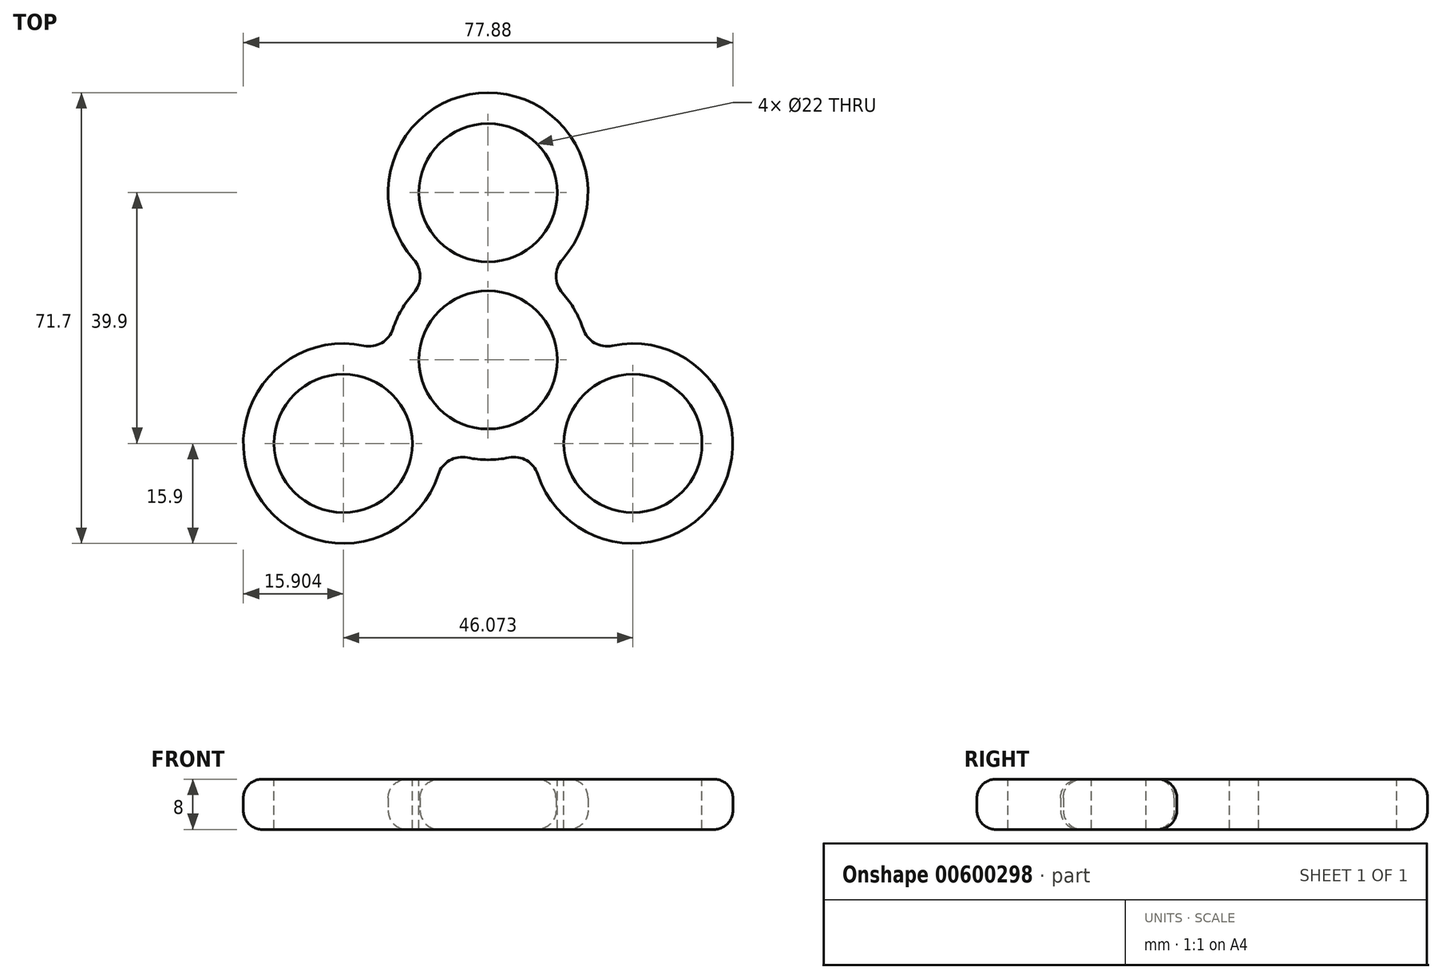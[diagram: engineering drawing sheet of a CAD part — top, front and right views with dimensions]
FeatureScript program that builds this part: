
annotation { "Feature Type Name" : "Feature", "Feature Type Description" : "" }
export const myFeature = defineFeature(function(context is Context, id is Id, definition is map)
    precondition{}
    {
        {
            var Q0;
            Q0=qCreatedBy(makeId("Top.planeOp"),FACE);
            var sketch = newSketch(context, id + "F0", { "sketchPlane" : qUnion([Q0])});
            skCircle(sketch, "E0", {"center": v(0, 0) * mm, "radius": 42.5 * mm, "construction": true});
            skArc(sketch, "E1", {"start": v(-11.83, 15.97) * mm, "mid": v(0, 42.5) * mm, "end": v(11.83, 15.97) * mm});
            skArc(sketch, "E2", {"start": v(19.75, 2.26) * mm, "mid": v(36.8, -21.25) * mm, "end": v(7.92, -18.23) * mm});
            skArc(sketch, "E3", {"start": v(-19.75, 2.26) * mm, "mid": v(-36.8, -21.25) * mm, "end": v(-7.92, -18.23) * mm});
            skLineSegment(sketch, "E4", {"start": v(0, 26.6) * mm, "end": v(0, 0) * mm, "construction": true});
            skLineSegment(sketch, "E5", {"start": v(0, 0) * mm, "end": v(-23.04, -13.3) * mm, "construction": true});
            skLineSegment(sketch, "E6", {"start": v(0, 0) * mm, "end": v(23.04, -13.3) * mm, "construction": true});
            skLineSegment(sketch, "E7", {"start": v(0, -53.2) * mm, "end": v(-46.07, 26.6) * mm, "construction": true});
            skLineSegment(sketch, "E8", {"start": v(0, -53.2) * mm, "end": v(46.07, 26.6) * mm, "construction": true});
            skLineSegment(sketch, "E9", {"start": v(-46.07, 26.6) * mm, "end": v(46.07, 26.6) * mm, "construction": true});
            skArc(sketch, "E10", {"start": v(-11.83, 15.97) * mm, "mid": v(-10.8, 13.3) * mm, "end": v(-11.83, 10.63) * mm});
            skArc(sketch, "E11", {"start": v(-19.75, 2.26) * mm, "mid": v(-16.92, 2.7) * mm, "end": v(-15.12, 4.93) * mm});
            skArc(sketch, "E12", {"start": v(11.83, 15.97) * mm, "mid": v(10.8, 13.3) * mm, "end": v(11.83, 10.63) * mm});
            skArc(sketch, "E13", {"start": v(19.75, 2.26) * mm, "mid": v(16.92, 2.7) * mm, "end": v(15.12, 4.93) * mm});
            skArc(sketch, "E14", {"start": v(11.83, 10.63) * mm, "mid": v(13.77, 7.95) * mm, "end": v(15.12, 4.93) * mm});
            skArc(sketch, "E15", {"start": v(-7.92, -18.23) * mm, "mid": v(-6.12, -16) * mm, "end": v(-3.29, -15.56) * mm});
            skArc(sketch, "E16", {"start": v(7.92, -18.23) * mm, "mid": v(6.12, -16) * mm, "end": v(3.29, -15.56) * mm});
            skArc(sketch, "E17", {"start": v(-3.29, -15.56) * mm, "mid": v(0, -15.9) * mm, "end": v(3.29, -15.56) * mm});
            skArc(sketch, "E18", {"start": v(-15.12, 4.93) * mm, "mid": v(-13.77, 7.95) * mm, "end": v(-11.83, 10.63) * mm});
            skSolve(sketch);
        }
        {
            var Q0;
            Q0 = qSketchRegion(id + "F0", true);
            extrude(context, id + "F1", {"entities" : qUnion([Q0]), "endBound" : BoundingType.SYMMETRIC, "depth" : 8 * mm, "offsetDistance" : 25 * mm});
        }
        {
            var Q0;
            Q0=qCreatedBy(makeId("Top.planeOp"),FACE);
            var sketch = newSketch(context, id + "F2", { "sketchPlane" : qUnion([Q0])});
            skLineSegment(sketch, "E19.0", {"start": v(-11.83, 15.97) * mm, "end": v(-11.83, 15.97) * mm});
            skLineSegment(sketch, "E20.0", {"start": v(-19.75, 2.26) * mm, "end": v(-19.75, 2.26) * mm});
            skLineSegment(sketch, "E21.0", {"start": v(19.75, 2.26) * mm, "end": v(19.75, 2.26) * mm});
            skCircle(sketch, "E22", {"center": v(0, 26.6) * mm, "radius": 11 * mm});
            skCircle(sketch, "E23", {"center": v(-23.04, -13.3) * mm, "radius": 11 * mm});
            skCircle(sketch, "E24", {"center": v(23.04, -13.3) * mm, "radius": 11 * mm});
            skCircle(sketch, "E25", {"center": v(0, 0) * mm, "radius": 11 * mm});
            skSolve(sketch);
        }
        {
            var Q0;
            Q0 = qSketchRegion(id + "F2", true);
            extrude(context, id + "F3", {"entities" : qUnion([Q0]), "operationType" : NewBodyOperationType.REMOVE, "endBound" : BoundingType.SYMMETRIC, "oppositeDirection" : true, "depth" : 9 * mm, "offsetDistance" : 25 * mm});
        }
        {
            var Q0;
            Q0=makeQuery(id+"F1.opExtrude","CAP_EDGE",EDGE,{"disambiguationData":[OSD([sQuery(id+"F0.wireOp",EDGE,"E15")])],"isStart":false});
            var Q1;
            Q1=makeQuery(id+"F1.opExtrude","CAP_EDGE",EDGE,{"disambiguationData":[OSD([sQuery(id+"F0.wireOp",EDGE,"E16")])],"isStart":true});
            fillet(context, id + "F4", {"entities" : qUnion([Q0, Q1]), "radius" : 3 * mm, "tangentPropagation" : true, "allowEdgeOverflow" : false});
        }
    });
